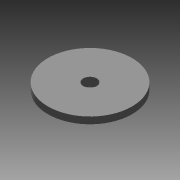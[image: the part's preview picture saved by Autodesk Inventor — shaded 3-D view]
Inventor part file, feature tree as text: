
AUTODESK INVENTOR PART (.ipt)
format: ipt  version: 2015 (Build 190159000, 159)  size: 88,576 bytes
history: native  units: mm
features: extrude x3, sketch x2
ambient origin geometry x8: Origin, YZ Plane, XZ Plane, XY Plane, X Axis, Y Axis, Z Axis, Center Point
bodies: Solid1 (feature_tree)
feature tree (5):
  sketch  "Sketch1"  dims[d0=25.0mm d1=8.0mm]
  extrude  "Extrusion1"  Depth=8.0mm
  extrude  "Extrusion2"  Depth=2.0mm TaperAngle=0.0deg
  extrude  "Extrusion3"  Depth=2.0mm TaperAngle=0.0deg
  sketch  "Sketch2"  dims[d2=11.0mm d3=2.0mm d4=0.0mm d5=2.0mm d6=0.0mm d7=4.0mm d8=2.0mm d9=0.0mm]
